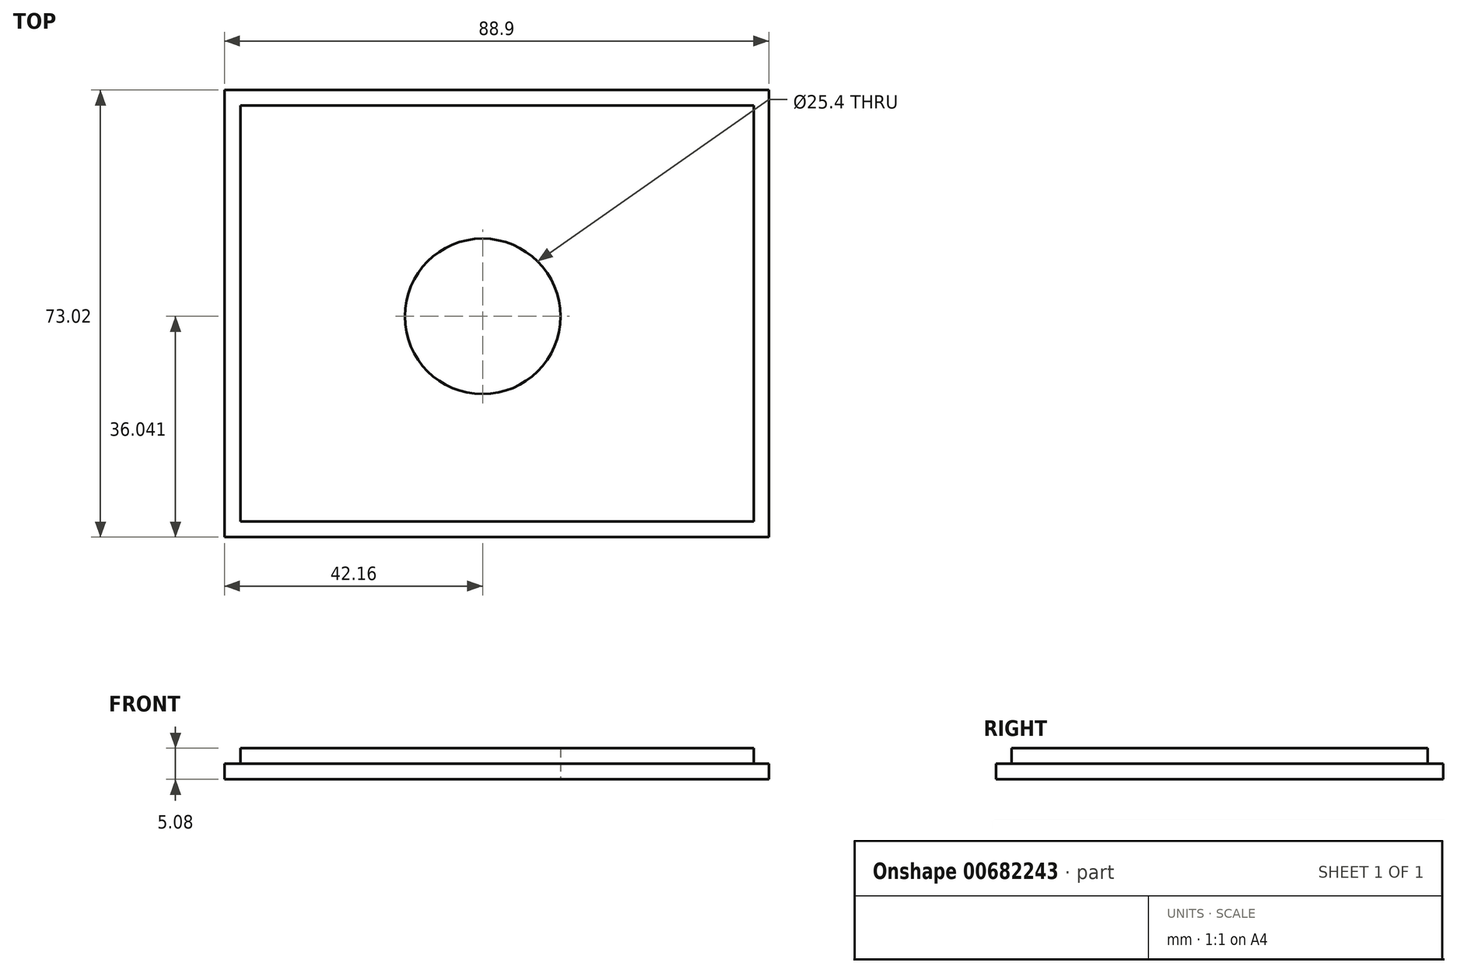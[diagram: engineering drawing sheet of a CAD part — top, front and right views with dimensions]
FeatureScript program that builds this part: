
annotation { "Feature Type Name" : "Feature", "Feature Type Description" : "" }
export const myFeature = defineFeature(function(context is Context, id is Id, definition is map)
    precondition{}
    {
        {
            var Q0;
            Q0=qCreatedBy(makeId("Top.planeOp"),FACE);
            var sketch = newSketch(context, id + "F0", { "sketchPlane" : qUnion([Q0])});
            skLineSegment(sketch, "E0.bottom", {"start": v(18.4, -1.62) * mm, "end": v(-70.5, -1.62) * mm});
            skLineSegment(sketch, "E0.top", {"start": v(18.4, -74.64) * mm, "end": v(-70.5, -74.64) * mm});
            skLineSegment(sketch, "E0.left", {"start": v(18.4, -1.62) * mm, "end": v(18.4, -74.64) * mm});
            skLineSegment(sketch, "E0.right", {"start": v(-70.5, -1.62) * mm, "end": v(-70.5, -74.64) * mm});
            skLineSegment(sketch, "E1", {"start": v(-67.88, -4.16) * mm, "end": v(-67.88, -72.1) * mm});
            skLineSegment(sketch, "E2", {"start": v(15.94, -4.16) * mm, "end": v(15.94, -72.1) * mm});
            skLineSegment(sketch, "E3", {"start": v(-67.88, -4.16) * mm, "end": v(15.94, -4.16) * mm});
            skLineSegment(sketch, "E4", {"start": v(-67.88, -72.1) * mm, "end": v(15.94, -72.1) * mm});
            skCircle(sketch, "E5", {"center": v(-28.34, -38.6) * mm, "radius": 12.7 * mm});
            skSolve(sketch);
        }
        {
            var Q0;
            Q0=makeQuery(id+"F0.imprint","IMPRINT",FACE,{"disambiguationData":[TD([[makeQuery(id+"F0.imprint","IMPRINT",EDGE,{"derivedFrom":sQuery(id+"F0.wireOp",EDGE,"E0.bottom")}),1.0]])]});
            extrude(context, id + "F1", {"entities" : qUnion([Q0]), "depth" : 2.54 * mm, "offsetDistance" : 25.4 * mm});
        }
        {
            var Q0;
            Q0=makeQuery(id+"F0.imprint","IMPRINT",FACE,{"disambiguationData":[TD([[makeQuery(id+"F0.imprint","IMPRINT",EDGE,{"derivedFrom":sQuery(id+"F0.wireOp",EDGE,"E1")}),1.0]])]});
            extrude(context, id + "F2", {"entities" : qUnion([Q0]), "operationType" : NewBodyOperationType.ADD, "depth" : 5.08 * mm, "offsetDistance" : 25.4 * mm});
        }
    });
